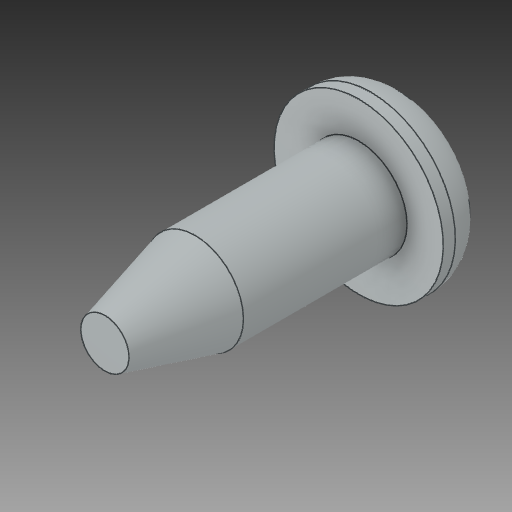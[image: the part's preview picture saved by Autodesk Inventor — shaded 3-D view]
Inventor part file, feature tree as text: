
AUTODESK INVENTOR PART (.ipt)
format: ipt  version: 2018 (Build 220112000, 112)  size: 158,720 bytes
history: native  units: mm
features: other x1, chamfer x1
ambient origin geometry x8: Origin, YZ Plane, XZ Plane, XY Plane, X Axis, Y Axis, Z Axis, Center Point
bodies: Body1 (feature_tree)
feature tree (2):
  other  "ソリッド1"
  chamfer  "Chamfer1"  [1 undecoded]
note: 1 required parameter value undecoded (feature->parameter linkage not recoverable at this tier; creation-order binding heuristic only, values carry confidence <= 0.55)
